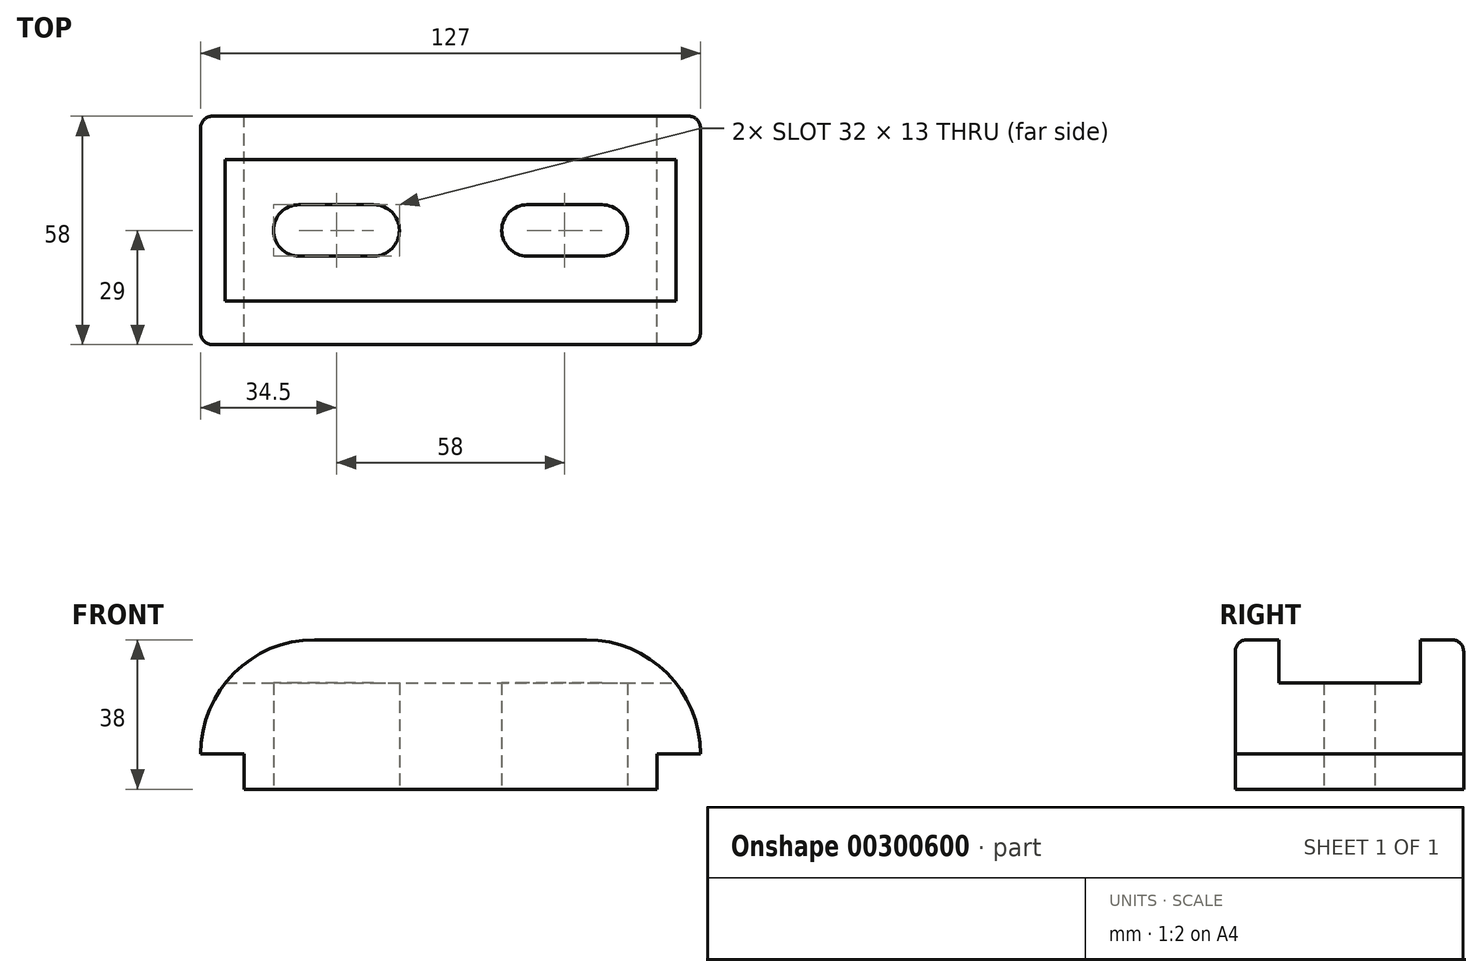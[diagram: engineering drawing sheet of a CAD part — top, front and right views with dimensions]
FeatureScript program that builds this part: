
annotation { "Feature Type Name" : "Feature", "Feature Type Description" : "" }
export const myFeature = defineFeature(function(context is Context, id is Id, definition is map)
    precondition{}
    {
        {
            var Q0;
            Q0=qCreatedBy(makeId("Front.planeOp"),FACE);
            var sketch = newSketch(context, id + "F0", { "sketchPlane" : qUnion([Q0])});
            skLineSegment(sketch, "E0", {"start": v(0, 0) * mm, "end": v(52.5, 0) * mm});
            skLineSegment(sketch, "E1", {"start": v(52.5, 0) * mm, "end": v(52.5, 9) * mm});
            skLineSegment(sketch, "E2", {"start": v(52.5, 9) * mm, "end": v(63.5, 9) * mm});
            skLineSegment(sketch, "E3", {"start": v(0, 38) * mm, "end": v(34.5, 38) * mm});
            skArc(sketch, "E4", {"start": v(63.5, 9) * mm, "mid": v(55, 29.5) * mm, "end": v(34.5, 38) * mm});
            skLineSegment(sketch, "E5", {"start": v(0, 68.75) * mm, "end": v(0, -20.55) * mm, "construction": true});
            skLineSegment(sketch, "E6.MirrorCS", {"start": v(0, 38) * mm, "end": v(-34.5, 38) * mm});
            skArc(sketch, "E7.MirrorCS", {"start": v(-63.5, 9) * mm, "mid": v(-55, 29.5) * mm, "end": v(-34.5, 38) * mm});
            skLineSegment(sketch, "E8.MirrorCS", {"start": v(-52.5, 9) * mm, "end": v(-63.5, 9) * mm});
            skLineSegment(sketch, "E9.MirrorCS", {"start": v(0, 0) * mm, "end": v(-52.5, 0) * mm});
            skLineSegment(sketch, "E10.MirrorCS", {"start": v(-52.5, 0) * mm, "end": v(-52.5, 9) * mm});
            skSolve(sketch);
        }
        {
            var Q0;
            Q0=makeQuery(id+"F0.imprint","IMPRINT",FACE,{"disambiguationData":[TD([[makeQuery(id+"F0.imprint","IMPRINT",EDGE,{"derivedFrom":sQuery(id+"F0.wireOp",EDGE,"E0")}),1.0]])]});
            extrude(context, id + "F1", {"entities" : qUnion([Q0]), "endBound" : BoundingType.SYMMETRIC, "depth" : 58 * mm});
        }
        {
            var Q0;
            Q0=makeQuery(id+"F1.opExtrude","CAP_EDGE",EDGE,{"disambiguationData":[OSD([sQuery(id+"F0.wireOp",EDGE,"E3"),sQuery(id+"F0.wireOp",EDGE,"E6.MirrorCS")])],"isStart":false});
            var Q1;
            Q1=makeQuery(id+"F1.opExtrude","CAP_EDGE",EDGE,{"disambiguationData":[OSD([sQuery(id+"F0.wireOp",EDGE,"E3"),sQuery(id+"F0.wireOp",EDGE,"E6.MirrorCS")])],"isStart":true});
            fillet(context, id + "F2", {"entities" : qUnion([Q0, Q1]), "radius" : 3 * mm, "tangentPropagation" : true, "allowEdgeOverflow" : false});
        }
        {
            var Q0;
            Q0=makeQuery(id+"F1.opExtrude","SWEPT_FACE",FACE,{"disambiguationData":[OSD([sQuery(id+"F0.wireOp",EDGE,"E3"),sQuery(id+"F0.wireOp",EDGE,"E6.MirrorCS")])]});
            var sketch = newSketch(context, id + "F3", { "sketchPlane" : qUnion([Q0])});
            skLineSegment(sketch, "E11.bottom", {"start": v(-63.5, 18) * mm, "end": v(63.5, 18) * mm});
            skLineSegment(sketch, "E11.top", {"start": v(-63.5, -18) * mm, "end": v(63.5, -18) * mm});
            skLineSegment(sketch, "E11.left", {"start": v(-63.5, 18) * mm, "end": v(-63.5, -18) * mm});
            skLineSegment(sketch, "E11.right", {"start": v(63.5, 18) * mm, "end": v(63.5, -18) * mm});
            skSolve(sketch);
        }
        {
            var Q0;
            Q0 = qSketchRegion(id + "F3", true);
            extrude(context, id + "F4", {"entities" : qUnion([Q0]), "operationType" : NewBodyOperationType.REMOVE, "oppositeDirection" : true, "depth" : 11 * mm});
        }
        {
            var Q0;
            Q0=qCreatedBy(makeId("Top.planeOp"),FACE);
            var sketch = newSketch(context, id + "F5", { "sketchPlane" : qUnion([Q0])});
            skLineSegment(sketch, "E12", {"start": v(-66.94, 0) * mm, "end": v(78.63, 0) * mm, "construction": true});
            skLineSegment(sketch, "E13", {"start": v(-38.5, 6.5) * mm, "end": v(-19.5, 6.5) * mm});
            skLineSegment(sketch, "E14", {"start": v(19.5, 6.5) * mm, "end": v(38.5, 6.5) * mm});
            skArc(sketch, "E15", {"start": v(-38.5, 6.5) * mm, "mid": v(-43.1, 4.6) * mm, "end": v(-45, 0) * mm});
            skArc(sketch, "E16", {"start": v(45, 0) * mm, "mid": v(43.1, 4.6) * mm, "end": v(38.5, 6.5) * mm});
            skArc(sketch, "E17", {"start": v(-13, 0) * mm, "mid": v(-14.9, 4.6) * mm, "end": v(-19.5, 6.5) * mm});
            skArc(sketch, "E18", {"start": v(19.5, 6.5) * mm, "mid": v(14.9, 4.6) * mm, "end": v(13, 0) * mm});
            skLineSegment(sketch, "E19.MirrorCS", {"start": v(-38.5, -6.5) * mm, "end": v(-19.5, -6.5) * mm});
            skArc(sketch, "E20.MirrorCS", {"start": v(-13, 0) * mm, "mid": v(-14.9, -4.6) * mm, "end": v(-19.5, -6.5) * mm});
            skArc(sketch, "E21.MirrorCS", {"start": v(-38.5, -6.5) * mm, "mid": v(-43.1, -4.6) * mm, "end": v(-45, 0) * mm});
            skLineSegment(sketch, "E22.MirrorCS", {"start": v(19.5, -6.5) * mm, "end": v(38.5, -6.5) * mm});
            skArc(sketch, "E23.MirrorCS", {"start": v(45, 0) * mm, "mid": v(43.1, -4.6) * mm, "end": v(38.5, -6.5) * mm});
            skArc(sketch, "E24.MirrorCS", {"start": v(19.5, -6.5) * mm, "mid": v(14.9, -4.6) * mm, "end": v(13, 0) * mm});
            skSolve(sketch);
        }
        {
            var Q0;
            Q0 = qSketchRegion(id + "F5", true);
            extrude(context, id + "F6", {"entities" : qUnion([Q0]), "operationType" : NewBodyOperationType.REMOVE, "endBound" : BoundingType.THROUGH_ALL, "depth" : 25 * mm});
        }
    });
